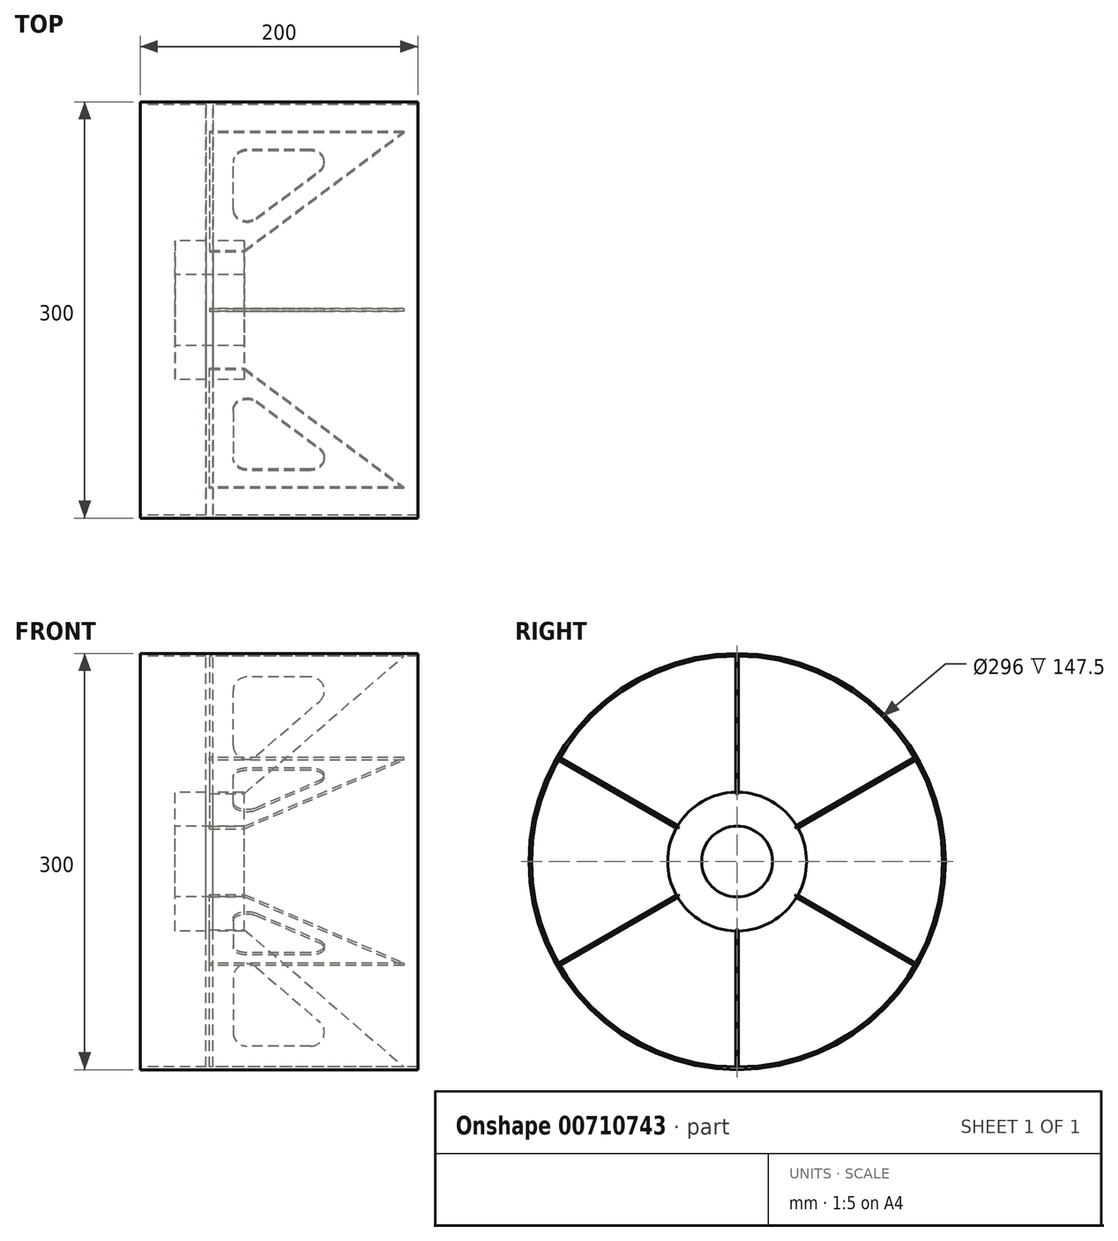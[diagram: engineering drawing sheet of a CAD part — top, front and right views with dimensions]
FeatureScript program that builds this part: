
annotation { "Feature Type Name" : "Feature", "Feature Type Description" : "" }
export const myFeature = defineFeature(function(context is Context, id is Id, definition is map)
    precondition{}
    {
        {
            var Q0;
            Q0=qCreatedBy(makeId("Right.planeOp"),FACE);
            var sketch = newSketch(context, id + "F0", { "sketchPlane" : qUnion([Q0])});
            skCircle(sketch, "E0", {"center": v(0, 0) * mm, "radius": 150 * mm});
            skCircle(sketch, "E1", {"center": v(0, 0) * mm, "radius": 148 * mm});
            skSolve(sketch);
        }
        {
            var Q0;
            Q0 = qSketchRegion(id + "F0", true);
            extrude(context, id + "F1", {"entities" : qUnion([Q0]), "depth" : 150 * mm, "offsetDistance" : 25 * mm, "hasSecondDirection" : true, "secondDirectionOppositeDirection" : true, "secondDirectionDepth" : 50 * mm});
        }
        {
            var Q0;
            Q0=qCreatedBy(makeId("Right.planeOp"),FACE);
            var sketch = newSketch(context, id + "F2", { "sketchPlane" : qUnion([Q0])});
            skCircle(sketch, "E2", {"center": v(0, 0) * mm, "radius": 148 * mm});
            skCircle(sketch, "E3", {"center": v(0, 0) * mm, "radius": 50 * mm});
            skSolve(sketch);
        }
        {
            var Q0;
            Q0 = qSketchRegion(id + "F2", true);
            extrude(context, id + "F3", {"entities" : qUnion([Q0]), "operationType" : NewBodyOperationType.ADD, "endBound" : BoundingType.SYMMETRIC, "depth" : 5 * mm, "offsetDistance" : 25 * mm});
        }
        {
            var Q0;
            Q0=qCreatedBy(makeId("Right.planeOp"),FACE);
            var sketch = newSketch(context, id + "F4", { "sketchPlane" : qUnion([Q0])});
            skCircle(sketch, "E4", {"center": v(0, 0) * mm, "radius": 50 * mm});
            skCircle(sketch, "E5", {"center": v(0, 0) * mm, "radius": 25.5 * mm});
            skSolve(sketch);
        }
        {
            var Q0;
            Q0 = qSketchRegion(id + "F4", true);
            extrude(context, id + "F5", {"entities" : qUnion([Q0]), "operationType" : NewBodyOperationType.ADD, "endBound" : BoundingType.SYMMETRIC, "depth" : 50 * mm, "offsetDistance" : 25 * mm});
        }
        {
            var Q0;
            Q0=qCreatedBy(makeId("Front.planeOp"),FACE);
            var sketch = newSketch(context, id + "F6", { "sketchPlane" : qUnion([Q0])});
            skLineSegment(sketch, "E6", {"start": v(140, 148) * mm, "end": v(0, 148) * mm});
            skLineSegment(sketch, "E7", {"start": v(0, 148) * mm, "end": v(0, 0) * mm});
            skLineSegment(sketch, "E8", {"start": v(0, 0) * mm, "end": v(0, 49) * mm});
            skLineSegment(sketch, "E9", {"start": v(0, 49) * mm, "end": v(25, 49) * mm});
            skLineSegment(sketch, "E10", {"start": v(25, 49) * mm, "end": v(140, 148) * mm});
            skLineSegment(sketch, "E11.0", {"start": v(72.64, 133) * mm, "end": v(26.99, 133) * mm});
            skLineSegment(sketch, "E11.1", {"start": v(33.51, 76.12) * mm, "end": v(79.16, 115.42) * mm});
            skLineSegment(sketch, "E12", {"start": v(16.99, 83.7) * mm, "end": v(16.99, 123) * mm});
            skPoint(sketch, "E13.visualSharp", {"position": v(99.58, 133) * mm});
            skArc(sketch, "E13.filletArc", {"start": v(79.16, 115.42) * mm, "mid": v(82.02, 126.48) * mm, "end": v(72.64, 133) * mm});
            skPoint(sketch, "E14.visualSharp", {"position": v(16.99, 133) * mm});
            skArc(sketch, "E14.filletArc", {"start": v(26.99, 133) * mm, "mid": v(19.92, 130.07) * mm, "end": v(16.99, 123) * mm});
            skPoint(sketch, "E15.visualSharp", {"position": v(16.99, 61.9) * mm});
            skArc(sketch, "E15.filletArc", {"start": v(16.99, 83.7) * mm, "mid": v(22.82, 74.61) * mm, "end": v(33.51, 76.12) * mm});
            skSolve(sketch);
        }
        {
            var Q0;
            Q0=makeQuery(id+"F6.imprint","IMPRINT",FACE,{"disambiguationData":[TD([[makeQuery(id+"F6.imprint","IMPRINT",EDGE,{"derivedFrom":sQuery(id+"F6.wireOp",EDGE,"E6")}),1.0]])]});
            extrude(context, id + "F7", {"entities" : qUnion([Q0]), "endBound" : BoundingType.SYMMETRIC, "depth" : 2 * mm, "offsetDistance" : 25 * mm});
        }
        {
            var Q0;
            Q0=makeQuery(id+"F7.opExtrude","SWEPT_BODY",BODY,{"disambiguationData":[OSD([sQuery(id+"F6.wireOp",EDGE,"E6"),sQuery(id+"F6.wireOp",EDGE,"E7"),sQuery(id+"F6.wireOp",EDGE,"E9"),sQuery(id+"F6.wireOp",EDGE,"E10")])]});
            var Q1;
            Q1=makeQuery(id+"F5.opExtrude","CAP_EDGE",EDGE,{"disambiguationData":[OSD([sQuery(id+"F4.wireOp",EDGE,"E5")])],"isStart":false});
            circularPattern(context, id + "F8", {"entities" : qUnion([Q0]), "axis" : qUnion([Q1]), "angle" : 360 * degree, "instanceCount" : 6, "equalSpace" : true});
        }
    });
